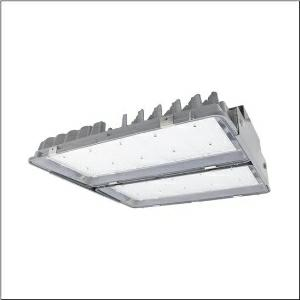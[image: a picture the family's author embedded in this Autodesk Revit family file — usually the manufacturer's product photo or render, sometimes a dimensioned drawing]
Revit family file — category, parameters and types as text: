
# Revit family: highbay_11xtreme_51hf81db4vma
name_source: partatom
category: Lighting Fixtures
units: mm (PartAtom-declared; Revit-internal decimal feet)

## family parameters
Cut with Voids When Loaded = No
Host = Face
Light Source = No
Part Type = Normal
Room Calculation Point = No
Round Connector Dimension = Use Diameter
Shared = No

## types (1)
- --- (1 x LED, 69400 lm, 380.2 W, 4000K)
    Apparent Load = 380 VA
    CIE Flux Codes = 88 96 99 100 100
    Color Rendering = 80
    Color Temperature = 4000K
    Default Elevation = 1800 mm
    Description = Highbay 11Xtreme, high bay luminaire, primary light control with lens, of PMMA, primary optical cover: cover, of toughened safety glass, light emission: direct distribution, primary light characteristic: symmetric, installation type: suspended mounting, surface-mounted, 2x LED module,for 1x 2x LED, rated luminous flux: 69.400lm, luminous efficacy: 183lm/W, light colour: 840, colour temperature: 4000K, control gear: DALI 2 (with two DALI addresses), with cable H07RN-F 5x 1.5mm², mains connection: 220..240V, AC, 50/60Hz, cable length: 1,5m, rated input power: 380W, luminaire housing, of diecast aluminium, partly coated, silver, length: 595mm, width: 560mm, height: 195mm, protection rating (complete): IP66, insulation class (complete): insulation class I (protective earthing), certification: CE, ENEC, UKCA, protection symbol: D, ball protection: ball impact resistant according to DIN VDE 0710 part 13 (with chain suspension), impact resistance: IK08, permissible operating ambient temperature: -25..+45°C, reducing of maximum allowable ambient temperature of 5°C with ceiling mounting, packaging unit: 1 piece
    Height = 157 mm
    Lamp = 1 x LED
    Lamp Light Flux = 69400 lm
    Lamp Power = 380.2 W
    Lamp count = 1
    Length = 593 mm
    Luminous efficacy = 183 lm/W
    Manufacturer = Siteco
    ModVariant = No
    Model = 51HF81DB4VMA
    Mounting Place = Ceiling
    Mounting Type = Pendant
    Number of Poles = 1
    OnlyDefault = Yes
    Power Factor = 1
    Product Name = Highbay 11Xtreme
    Product group = high bay luminaire
    ProductGroupID = 902
    Protection Class = Protection class I
    Protection Degree = IP 66
    RLX_Detail_Level = 1
    RLX_Emergency_Light_Flux = 0 lm
    RLX_Emergency_Type = 0
    RLX_Emergency_Type_DB = No
    RlxData = <blob elided: 33837 chars, md5=6ebdabd2>
    Socket = socket
    Standby Power = 0 W
    System Light Flux = 69402 lm
    System Power = 380 W
    Type Comments = factory setting: luminous flux: 100 % | dim-lin: 254 | 1257 mA
    Type Image = l_1258340.jpg
    URL = http://relux.com
    VarID = @adj_084477
    Voltage = 0 V
    Weight = 0.00 kg
    Width = 568 mm

## geometry (parser evidence)
native form markers: Blend x4, Sweep x10
no freeform markers — native parametric forms only
